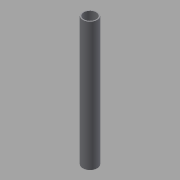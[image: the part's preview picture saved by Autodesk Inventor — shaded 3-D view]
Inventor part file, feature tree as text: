
AUTODESK INVENTOR PART (.ipt)
format: ipt  version: 2014 (Build 180170000, 170)  size: 86,016 bytes
history: native  units: mm
features: extrude x1, sketch x1
ambient origin geometry x8: Origin, YZ Plane, XZ Plane, XY Plane, X Axis, Y Axis, Z Axis, Center Point
bodies: Solid1 (feature_tree)
feature tree (2):
  extrude  "Extrusion1"  Depth=250.0mm
  sketch  "Sketch1"  dims[d0=24.0mm d1=2.0mm d2=250.0mm d3=0.0mm]
